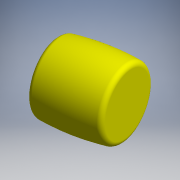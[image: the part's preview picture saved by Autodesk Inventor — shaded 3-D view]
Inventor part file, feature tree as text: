
AUTODESK INVENTOR PART (.ipt)
format: ipt  version: 2017.3 (Build 213256000, 256)  size: 128,000 bytes
history: native  units: mm (DEFAULTED — no unit token found)
features: other x14, revolve x1, sketch x1
ambient origin geometry x8: Origin, YZ Plane, XZ Plane, XY Plane, X Axis, Y Axis, Z Axis, Center Point
bodies: Solid1 (feature_tree)
feature tree (16):
  revolve  "Revolution1"  [1 undecoded]
  other  "NO_GEO_XY"
  other  "NO_GEO_YZ"
  other  "NO_GEO_ZX"
  other  "NO_GEO_X"
  other  "NO_GEO_Y"
  other  "NO_GEO_Z"
  other  "NO_GEO_Center"
  other  "roller2_XY"
  other  "roller2_YZ"
  other  "roller2_ZX"
  other  "roller2_X"
  other  "roller2_Y"
  other  "roller2_Z"
  other  "roller2_Center"
  sketch  "Sketch_1"  dims[d0=360.0deg]
note: 1 required parameter value undecoded (feature->parameter linkage not recoverable at this tier; creation-order binding heuristic only, values carry confidence <= 0.55)
